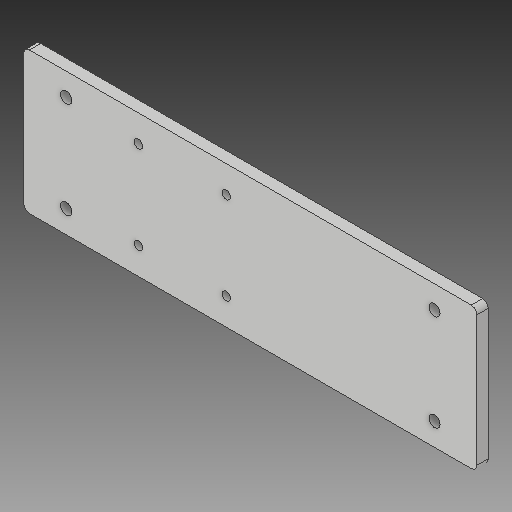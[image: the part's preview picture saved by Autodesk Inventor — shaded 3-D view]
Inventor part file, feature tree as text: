
AUTODESK INVENTOR PART (.ipt)
format: ipt  version: 2019 (Build 230136000, 136)  size: 131,072 bytes
history: native  units: in
note: dims shown in document units (in); Inventor stores cm internally (conversion verified against a paired STEP export)
features: reference x7, other x4, extrude x2, sketch x2, fillet x1, helix x1
ambient origin geometry x8: Origin, YZ Plane, XZ Plane, XY Plane, X Axis, Y Axis, Z Axis, Center Point
bodies: Solid1 (feature_tree)
feature tree (17):
  extrude  "Extrusion1"  Depth=0.1575in TaperAngle=0.0deg
  fillet  "Fillet1"  Radius=0.0787in
  extrude  "Extrusion2"  Depth=0.1575in
  sketch  "Sketch1"  dims[d0=1.9685in d1=0.1575in d2=0.0in d3=0.0787in]
  reference  "Reference1"
  sketch  "Sketch2"  dims[d4=0.1575in d5=0.1575in d6=0.1181in d7=0.1181in d8=0.1181in d9=0.1181in d10=0.1575in d11=0.1575in d12=0.315in d13=0.315in d14=0.315in d15=0.315in d16=0.1575in d17=0.0in]
  reference  "Reference2"
  reference  "Reference3"
  reference  "Reference4"
  reference  "Reference5"
  reference  "Reference6"
  reference  "Reference7"
  other  "<userpath>\Documents\CAD Files\Helix DLP\Helix DLP.iam"
  helix  "Helix DLP.iam"  [1 undecoded]
  other  "30X30 - T-slot - Aluminium Profile:3"
  other  "30X30 - T-slot - Aluminium Profile:1"
  other  "M1173041- NEMA 17 Screw rod:2"
note: 1 required parameter value undecoded (feature->parameter linkage not recoverable at this tier; creation-order binding heuristic only, values carry confidence <= 0.55)
